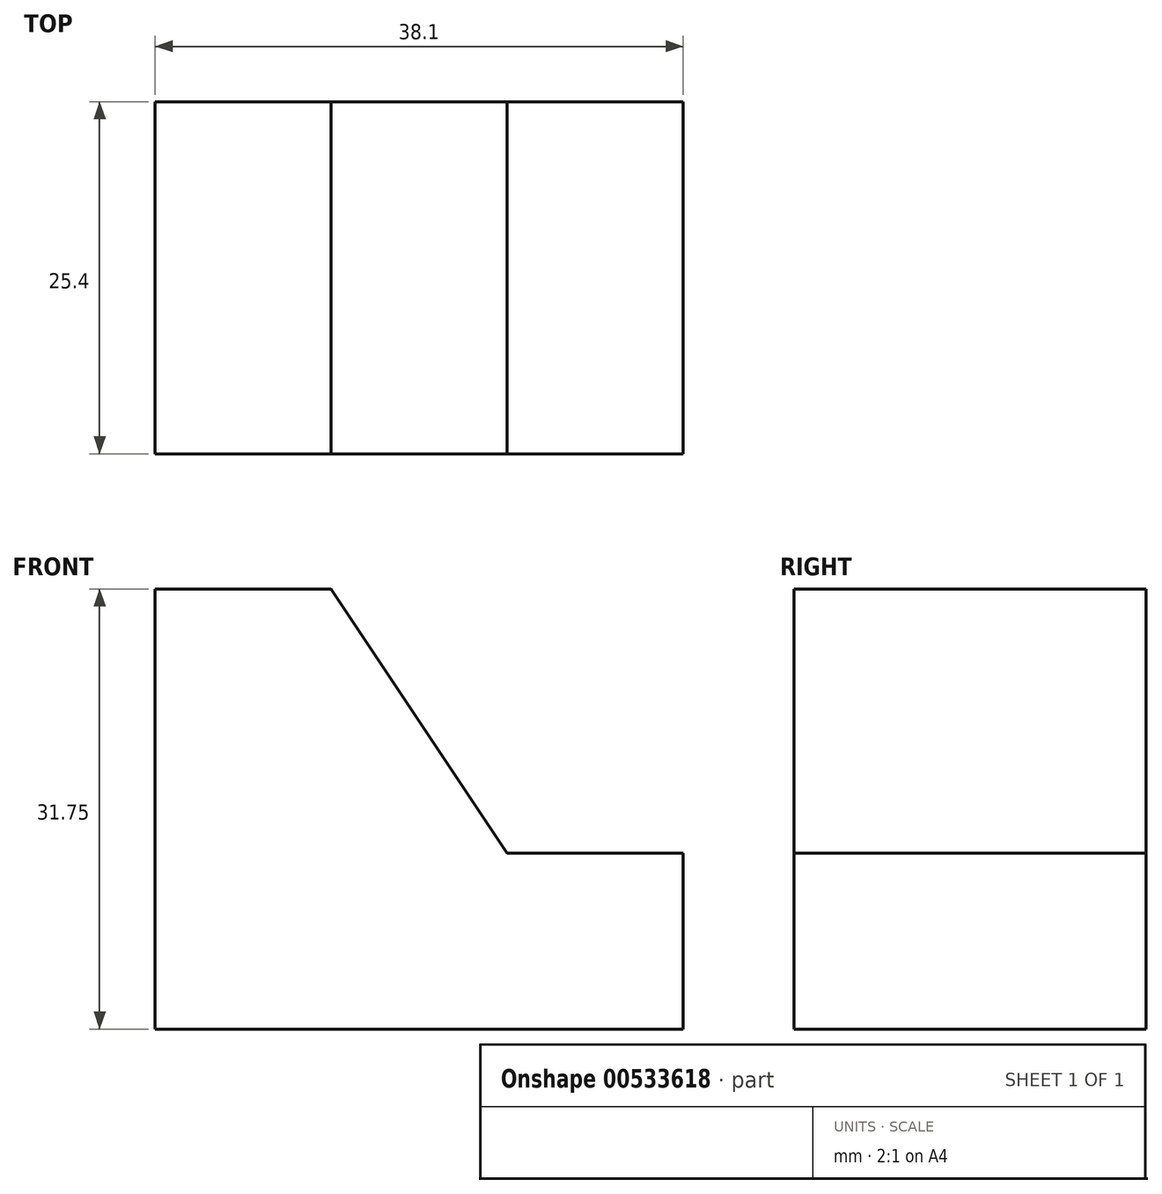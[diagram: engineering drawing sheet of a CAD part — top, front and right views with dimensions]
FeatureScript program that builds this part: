
annotation { "Feature Type Name" : "Feature", "Feature Type Description" : "" }
export const myFeature = defineFeature(function(context is Context, id is Id, definition is map)
    precondition{}
    {
        {
            var Q0;
            Q0=qCreatedBy(makeId("Front.planeOp"),FACE);
            var sketch = newSketch(context, id + "F0", { "sketchPlane" : qUnion([Q0])});
            skLineSegment(sketch, "E0", {"start": v(-54.54, 40.19) * mm, "end": v(-54.54, 8.44) * mm});
            skLineSegment(sketch, "E1", {"start": v(-54.54, 8.44) * mm, "end": v(-16.44, 8.44) * mm});
            skLineSegment(sketch, "E2", {"start": v(-16.44, 8.44) * mm, "end": v(-16.44, 21.14) * mm});
            skLineSegment(sketch, "E3", {"start": v(-16.44, 21.14) * mm, "end": v(-29.14, 21.14) * mm});
            skLineSegment(sketch, "E4", {"start": v(-54.54, 40.19) * mm, "end": v(-41.84, 40.19) * mm});
            skLineSegment(sketch, "E5", {"start": v(-41.84, 40.19) * mm, "end": v(-29.14, 21.14) * mm});
            skSolve(sketch);
        }
        {
            var Q0;
            Q0 = qSketchRegion(id + "F0", true);
            extrude(context, id + "F1", {"entities" : qUnion([Q0]), "depth" : 25.4 * mm, "offsetDistance" : 25.4 * mm});
        }
    });
